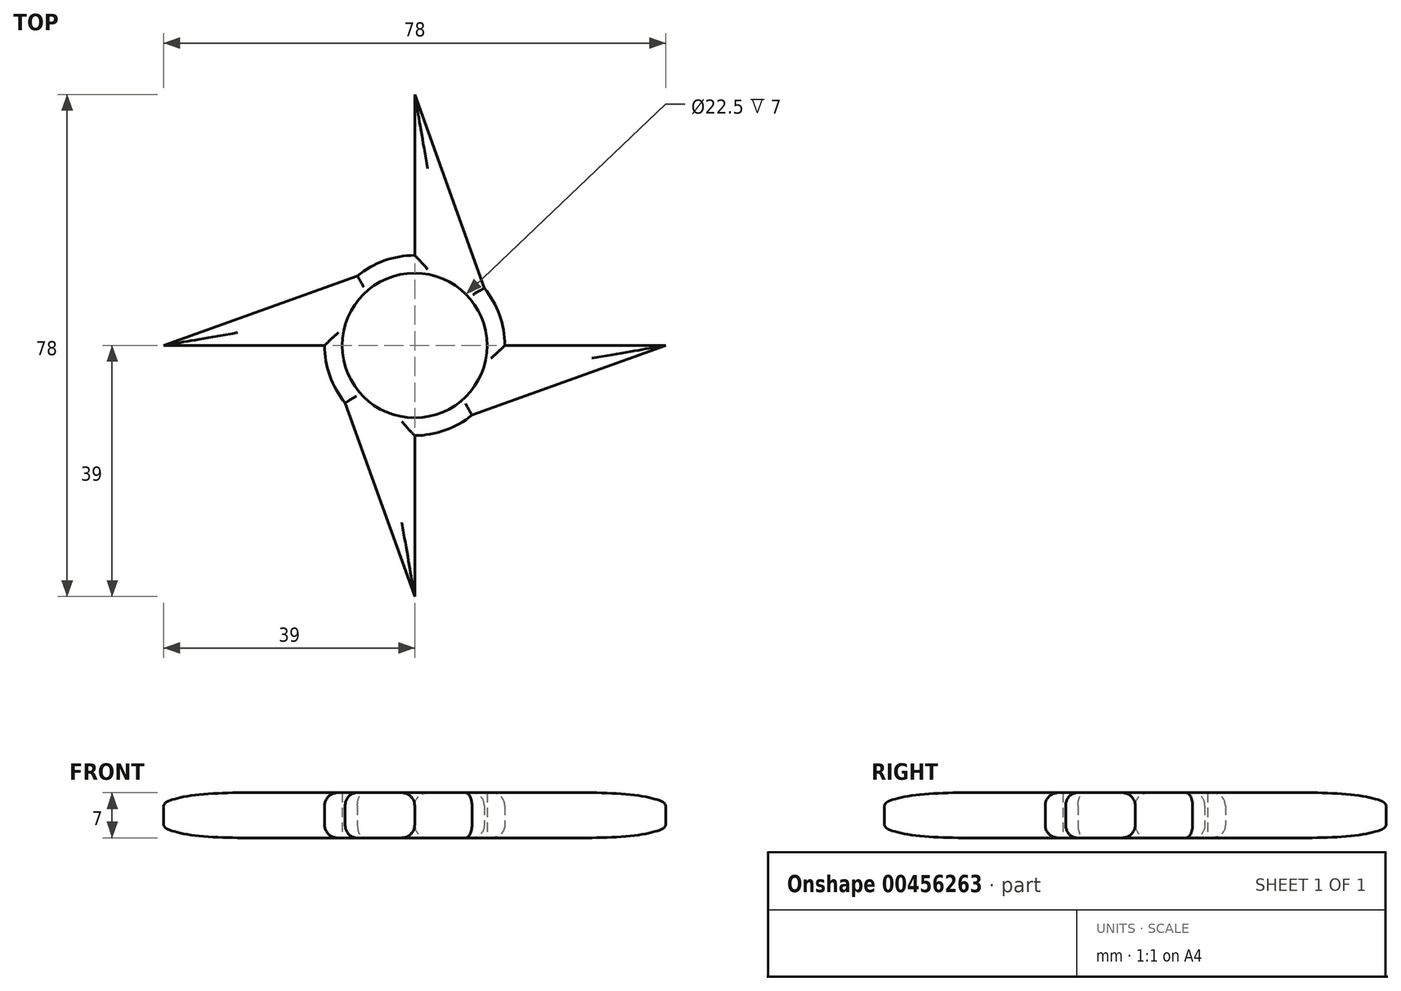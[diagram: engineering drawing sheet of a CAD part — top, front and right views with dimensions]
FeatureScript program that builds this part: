
annotation { "Feature Type Name" : "Feature", "Feature Type Description" : "" }
export const myFeature = defineFeature(function(context is Context, id is Id, definition is map)
    precondition{}
    {
        {
            var Q0;
            Q0=qCreatedBy(makeId("Top.planeOp"),FACE);
            var sketch = newSketch(context, id + "F0", { "sketchPlane" : qUnion([Q0])});
            skCircle(sketch, "E0", {"center": v(0, 0) * mm, "radius": 11.25 * mm});
            skCircle(sketch, "E1", {"center": v(0, 0) * mm, "radius": 14 * mm});
            skLineSegment(sketch, "E2", {"start": v(0, 14) * mm, "end": v(0, 39) * mm});
            skLineSegment(sketch, "E3", {"start": v(0, 39) * mm, "end": v(14, 0) * mm});
            skLineSegment(sketch, "E4", {"start": v(14, 0) * mm, "end": v(39, 0) * mm});
            skLineSegment(sketch, "E5", {"start": v(39, 0) * mm, "end": v(0, -14) * mm});
            skLineSegment(sketch, "E6", {"start": v(0, -14) * mm, "end": v(0, -39) * mm});
            skLineSegment(sketch, "E7", {"start": v(0, -39) * mm, "end": v(-14, 0) * mm});
            skLineSegment(sketch, "E8", {"start": v(-14, 0) * mm, "end": v(-39, 0) * mm});
            skLineSegment(sketch, "E9", {"start": v(-39, 0) * mm, "end": v(0, 14) * mm});
            skSolve(sketch);
        }
        {
            var Q0;
            {var subQ0=sQuery(id+"F0.wireOp",EDGE,"E8");Q0=makeQuery(id+"F0.imprint","IMPRINT",FACE,{"disambiguationData":[TD([[makeQuery(id+"F0.imprint","IMPRINT",EDGE,{"derivedFrom":subQ0}),-1.0]])]});}
            var Q1;
            Q1=makeQuery(id+"F0.imprint","IMPRINT",FACE,{"disambiguationData":[TD([[makeQuery(id+"F0.imprint","IMPRINT",EDGE,{"derivedFrom":sQuery(id+"F0.wireOp",EDGE,"E0")}),-1.0]])]});
            var Q2;
            {var subQ0=sQuery(id+"F0.wireOp",EDGE,"E2");Q2=makeQuery(id+"F0.imprint","IMPRINT",FACE,{"disambiguationData":[TD([[makeQuery(id+"F0.imprint","IMPRINT",EDGE,{"derivedFrom":subQ0}),-1.0]])]});}
            var Q3;
            {var subQ0=sQuery(id+"F0.wireOp",EDGE,"E6");Q3=makeQuery(id+"F0.imprint","IMPRINT",FACE,{"disambiguationData":[TD([[makeQuery(id+"F0.imprint","IMPRINT",EDGE,{"derivedFrom":subQ0}),-1.0]])]});}
            var Q4;
            {var subQ0=sQuery(id+"F0.wireOp",EDGE,"E4");Q4=makeQuery(id+"F0.imprint","IMPRINT",FACE,{"disambiguationData":[TD([[makeQuery(id+"F0.imprint","IMPRINT",EDGE,{"derivedFrom":subQ0}),-1.0]])]});}
            var Q5;
            {var subQ0=sQuery(id+"F0.wireOp",EDGE,"E7");var subQ1=sQuery(id+"F0.wireOp",EDGE,"E1");var subQ3=makeQuery(id+"F0.imprint","INTERSECT",VERTEX,{"derivedFrom":[subQ1,subQ0]});Q5=makeQuery(id+"F0.imprint","IMPRINT",FACE,{"disambiguationData":[TD([[makeQuery(id+"F0.imprint","IMPRINT",EDGE,{"disambiguationData":[TD([[subQ3,1.0]])],"derivedFrom":subQ1}),1.0]])]});}
            var Q6;
            {var subQ0=sQuery(id+"F0.wireOp",EDGE,"E5");var subQ1=sQuery(id+"F0.wireOp",EDGE,"E1");var subQ3=makeQuery(id+"F0.imprint","INTERSECT",VERTEX,{"derivedFrom":[subQ1,subQ0]});Q6=makeQuery(id+"F0.imprint","IMPRINT",FACE,{"disambiguationData":[TD([[makeQuery(id+"F0.imprint","IMPRINT",EDGE,{"disambiguationData":[TD([[subQ3,1.0]])],"derivedFrom":subQ1}),1.0]])]});}
            var Q7;
            {var subQ0=sQuery(id+"F0.wireOp",EDGE,"E3");var subQ1=sQuery(id+"F0.wireOp",EDGE,"E1");var subQ3=makeQuery(id+"F0.imprint","INTERSECT",VERTEX,{"derivedFrom":[subQ1,subQ0]});Q7=makeQuery(id+"F0.imprint","IMPRINT",FACE,{"disambiguationData":[TD([[makeQuery(id+"F0.imprint","IMPRINT",EDGE,{"disambiguationData":[TD([[subQ3,1.0]])],"derivedFrom":subQ1}),1.0]])]});}
            var Q8;
            {var subQ0=sQuery(id+"F0.wireOp",EDGE,"E9");var subQ1=sQuery(id+"F0.wireOp",EDGE,"E1");var subQ3=makeQuery(id+"F0.imprint","INTERSECT",VERTEX,{"derivedFrom":[subQ1,subQ0]});Q8=makeQuery(id+"F0.imprint","IMPRINT",FACE,{"disambiguationData":[TD([[makeQuery(id+"F0.imprint","IMPRINT",EDGE,{"disambiguationData":[TD([[subQ3,1.0]])],"derivedFrom":subQ1}),1.0]])]});}
            extrude(context, id + "F1", {"entities" : qUnion([Q0, Q1, Q2, Q3, Q4, Q5, Q6, Q7, Q8]), "depth" : 7 * mm});
        }
        {
            var Q0;
            Q0=makeQuery(id+"F1.opExtrude","CAP_EDGE",EDGE,{"disambiguationData":[OSD([sQuery(id+"F0.wireOp",EDGE,"E6")])],"isStart":false});
            var Q1;
            Q1=makeQuery(id+"F1.opExtrude","CAP_EDGE",EDGE,{"disambiguationData":[OSD([sQuery(id+"F0.wireOp",EDGE,"E5")])],"isStart":false});
            var Q2;
            Q2=makeQuery(id+"F1.opExtrude","CAP_EDGE",EDGE,{"disambiguationData":[OSD([sQuery(id+"F0.wireOp",EDGE,"E3")])],"isStart":false});
            var Q3;
            Q3=makeQuery(id+"F1.opExtrude","CAP_EDGE",EDGE,{"disambiguationData":[OSD([sQuery(id+"F0.wireOp",EDGE,"E9")])],"isStart":false});
            var Q4;
            Q4=makeQuery(id+"F1.opExtrude","CAP_EDGE",EDGE,{"disambiguationData":[OSD([sQuery(id+"F0.wireOp",EDGE,"E8")])],"isStart":false});
            var Q5;
            Q5=makeQuery(id+"F1.opExtrude","CAP_EDGE",EDGE,{"disambiguationData":[OSD([sQuery(id+"F0.wireOp",EDGE,"E7")])],"isStart":false});
            var Q6;
            Q6=makeQuery(id+"F1.opExtrude","CAP_EDGE",EDGE,{"disambiguationData":[OSD([sQuery(id+"F0.wireOp",EDGE,"E2")])],"isStart":false});
            var Q7;
            {var subQ0=sQuery(id+"F0.wireOp",EDGE,"E3");var subQ1=sQuery(id+"F0.wireOp",EDGE,"E1");Q7=makeQuery(id+"F1.opExtrude","CAP_EDGE",EDGE,{"disambiguationData":[OSD([subQ1]),TDD([makeQuery(id+"F0.imprint","IMPRINT",EDGE,{"disambiguationData":[TD([[makeQuery(id+"F0.imprint","INTERSECT",VERTEX,{"derivedFrom":[subQ1,subQ0]}),1.0]])],"derivedFrom":subQ1})])],"isStart":false});}
            var Q8;
            {var subQ0=sQuery(id+"F0.wireOp",EDGE,"E9");var subQ1=sQuery(id+"F0.wireOp",EDGE,"E1");Q8=makeQuery(id+"F1.opExtrude","CAP_EDGE",EDGE,{"disambiguationData":[OSD([subQ1]),TDD([makeQuery(id+"F0.imprint","IMPRINT",EDGE,{"disambiguationData":[TD([[makeQuery(id+"F0.imprint","INTERSECT",VERTEX,{"derivedFrom":[subQ1,subQ0]}),1.0]])],"derivedFrom":subQ1})])],"isStart":false});}
            var Q9;
            {var subQ0=sQuery(id+"F0.wireOp",EDGE,"E7");var subQ1=sQuery(id+"F0.wireOp",EDGE,"E1");Q9=makeQuery(id+"F1.opExtrude","CAP_EDGE",EDGE,{"disambiguationData":[OSD([subQ1]),TDD([makeQuery(id+"F0.imprint","IMPRINT",EDGE,{"disambiguationData":[TD([[makeQuery(id+"F0.imprint","INTERSECT",VERTEX,{"derivedFrom":[subQ1,subQ0]}),1.0]])],"derivedFrom":subQ1})])],"isStart":false});}
            var Q10;
            {var subQ0=sQuery(id+"F0.wireOp",EDGE,"E5");var subQ1=sQuery(id+"F0.wireOp",EDGE,"E1");Q10=makeQuery(id+"F1.opExtrude","CAP_EDGE",EDGE,{"disambiguationData":[OSD([subQ1]),TDD([makeQuery(id+"F0.imprint","IMPRINT",EDGE,{"disambiguationData":[TD([[makeQuery(id+"F0.imprint","INTERSECT",VERTEX,{"derivedFrom":[subQ1,subQ0]}),1.0]])],"derivedFrom":subQ1})])],"isStart":false});}
            var Q11;
            Q11=makeQuery(id+"F1.opExtrude","CAP_EDGE",EDGE,{"disambiguationData":[OSD([sQuery(id+"F0.wireOp",EDGE,"E4")])],"isStart":false});
            fillet(context, id + "F2", {"entities" : qUnion([Q0, Q1, Q2, Q3, Q4, Q5, Q6, Q7, Q8, Q9, Q10, Q11]), "radius" : 2 * mm, "tangentPropagation" : true, "allowEdgeOverflow" : false});
        }
        {
            var Q0;
            Q0=makeQuery(id+"F1.opExtrude","CAP_EDGE",EDGE,{"disambiguationData":[OSD([sQuery(id+"F0.wireOp",EDGE,"E8")])],"isStart":true});
            var Q1;
            Q1=makeQuery(id+"F1.opExtrude","CAP_EDGE",EDGE,{"disambiguationData":[OSD([sQuery(id+"F0.wireOp",EDGE,"E7")])],"isStart":true});
            var Q2;
            Q2=makeQuery(id+"F1.opExtrude","CAP_EDGE",EDGE,{"disambiguationData":[OSD([sQuery(id+"F0.wireOp",EDGE,"E6")])],"isStart":true});
            var Q3;
            Q3=makeQuery(id+"F1.opExtrude","CAP_EDGE",EDGE,{"disambiguationData":[OSD([sQuery(id+"F0.wireOp",EDGE,"E5")])],"isStart":true});
            var Q4;
            Q4=makeQuery(id+"F1.opExtrude","CAP_EDGE",EDGE,{"disambiguationData":[OSD([sQuery(id+"F0.wireOp",EDGE,"E4")])],"isStart":true});
            var Q5;
            Q5=makeQuery(id+"F1.opExtrude","CAP_EDGE",EDGE,{"disambiguationData":[OSD([sQuery(id+"F0.wireOp",EDGE,"E3")])],"isStart":true});
            var Q6;
            Q6=makeQuery(id+"F1.opExtrude","CAP_EDGE",EDGE,{"disambiguationData":[OSD([sQuery(id+"F0.wireOp",EDGE,"E2")])],"isStart":true});
            var Q7;
            Q7=makeQuery(id+"F1.opExtrude","CAP_EDGE",EDGE,{"disambiguationData":[OSD([sQuery(id+"F0.wireOp",EDGE,"E9")])],"isStart":true});
            var Q8;
            {var subQ0=sQuery(id+"F0.wireOp",EDGE,"E5");var subQ1=sQuery(id+"F0.wireOp",EDGE,"E1");Q8=makeQuery(id+"F1.opExtrude","CAP_EDGE",EDGE,{"disambiguationData":[OSD([subQ1]),TDD([makeQuery(id+"F0.imprint","IMPRINT",EDGE,{"disambiguationData":[TD([[makeQuery(id+"F0.imprint","INTERSECT",VERTEX,{"derivedFrom":[subQ1,subQ0]}),1.0]])],"derivedFrom":subQ1})])],"isStart":true});}
            var Q9;
            {var subQ0=sQuery(id+"F0.wireOp",EDGE,"E7");var subQ1=sQuery(id+"F0.wireOp",EDGE,"E1");Q9=makeQuery(id+"F1.opExtrude","CAP_EDGE",EDGE,{"disambiguationData":[OSD([subQ1]),TDD([makeQuery(id+"F0.imprint","IMPRINT",EDGE,{"disambiguationData":[TD([[makeQuery(id+"F0.imprint","INTERSECT",VERTEX,{"derivedFrom":[subQ1,subQ0]}),1.0]])],"derivedFrom":subQ1})])],"isStart":true});}
            var Q10;
            {var subQ0=sQuery(id+"F0.wireOp",EDGE,"E9");var subQ1=sQuery(id+"F0.wireOp",EDGE,"E1");Q10=makeQuery(id+"F1.opExtrude","CAP_EDGE",EDGE,{"disambiguationData":[OSD([subQ1]),TDD([makeQuery(id+"F0.imprint","IMPRINT",EDGE,{"disambiguationData":[TD([[makeQuery(id+"F0.imprint","INTERSECT",VERTEX,{"derivedFrom":[subQ1,subQ0]}),1.0]])],"derivedFrom":subQ1})])],"isStart":true});}
            var Q11;
            {var subQ0=sQuery(id+"F0.wireOp",EDGE,"E3");var subQ1=sQuery(id+"F0.wireOp",EDGE,"E1");Q11=makeQuery(id+"F1.opExtrude","CAP_EDGE",EDGE,{"disambiguationData":[OSD([subQ1]),TDD([makeQuery(id+"F0.imprint","IMPRINT",EDGE,{"disambiguationData":[TD([[makeQuery(id+"F0.imprint","INTERSECT",VERTEX,{"derivedFrom":[subQ1,subQ0]}),1.0]])],"derivedFrom":subQ1})])],"isStart":true});}
            fillet(context, id + "F3", {"entities" : qUnion([Q0, Q1, Q2, Q3, Q4, Q5, Q6, Q7, Q8, Q9, Q10, Q11]), "radius" : 2 * mm, "tangentPropagation" : true, "allowEdgeOverflow" : false});
        }
    });
